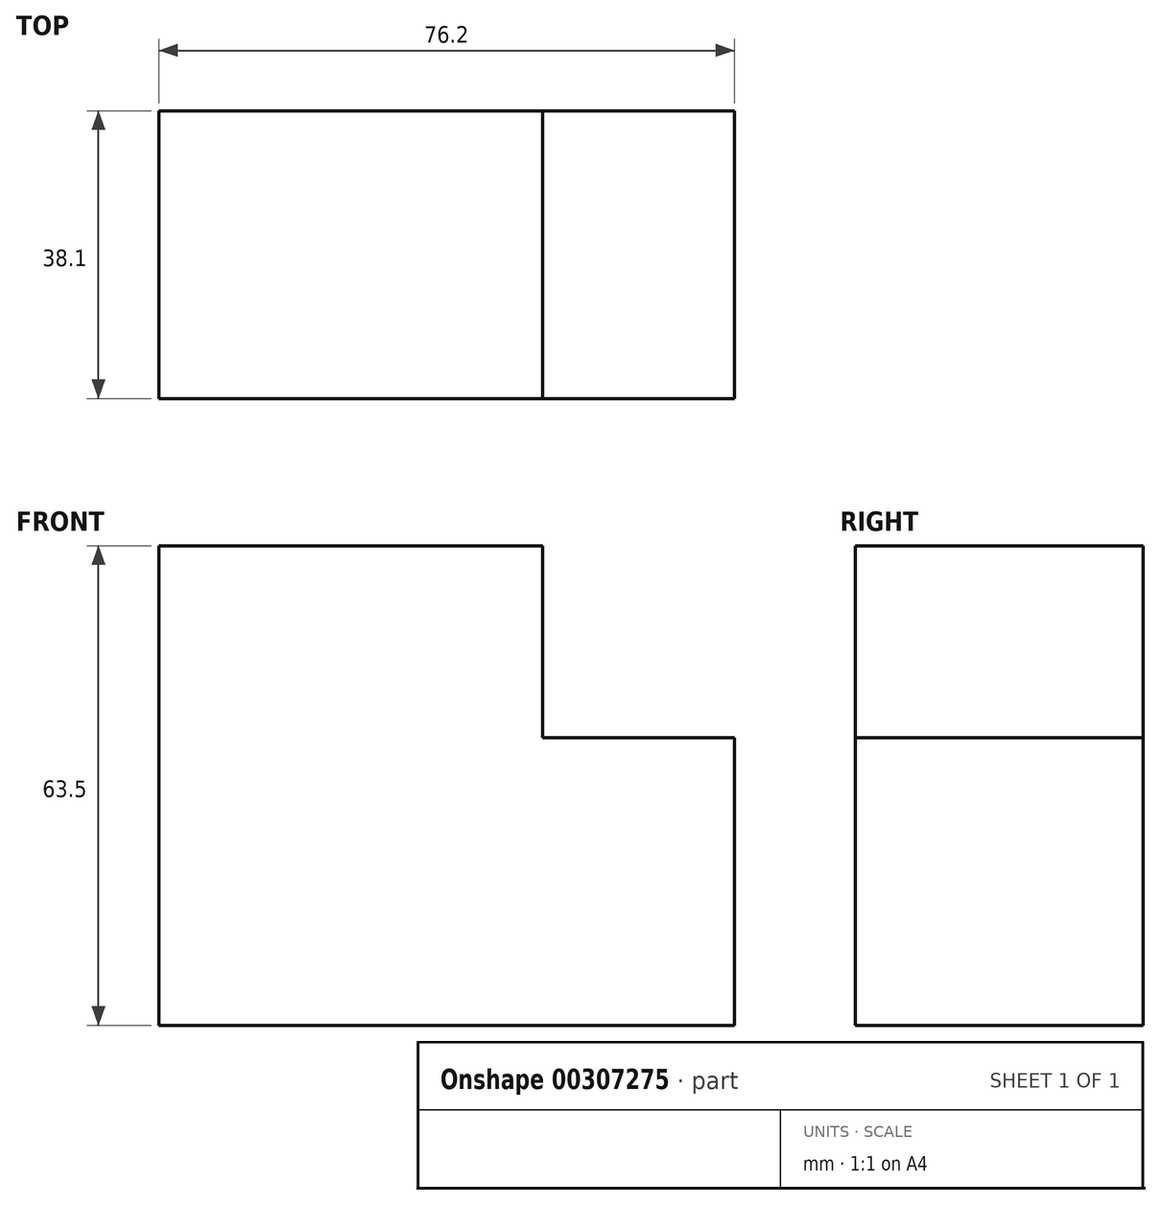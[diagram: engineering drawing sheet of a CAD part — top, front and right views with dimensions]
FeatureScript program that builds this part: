
annotation { "Feature Type Name" : "Feature", "Feature Type Description" : "" }
export const myFeature = defineFeature(function(context is Context, id is Id, definition is map)
    precondition{}
    {
        {
            var Q0;
            Q0=qCreatedBy(makeId("Front.planeOp"),FACE);
            var sketch = newSketch(context, id + "F0", { "sketchPlane" : qUnion([Q0])});
            skLineSegment(sketch, "E0", {"start": v(-34.28, -41.67) * mm, "end": v(41.92, -41.67) * mm});
            skLineSegment(sketch, "E1", {"start": v(41.92, -41.67) * mm, "end": v(41.92, -3.57) * mm});
            skLineSegment(sketch, "E2", {"start": v(41.92, -3.57) * mm, "end": v(16.52, -3.57) * mm});
            skLineSegment(sketch, "E3", {"start": v(16.52, -3.57) * mm, "end": v(16.52, 21.83) * mm});
            skLineSegment(sketch, "E4", {"start": v(16.52, 21.83) * mm, "end": v(-34.28, 21.83) * mm});
            skLineSegment(sketch, "E5", {"start": v(-34.28, 21.83) * mm, "end": v(-34.28, -41.67) * mm});
            skSolve(sketch);
        }
        {
            var Q0;
            Q0=makeQuery(id+"F0.imprint","IMPRINT",FACE,{"disambiguationData":[TD([[makeQuery(id+"F0.imprint","IMPRINT",EDGE,{"derivedFrom":sQuery(id+"F0.wireOp",EDGE,"E0")}),1.0]])]});
            extrude(context, id + "F1", {"entities" : qUnion([Q0]), "depth" : 38.1 * mm});
        }
    });
